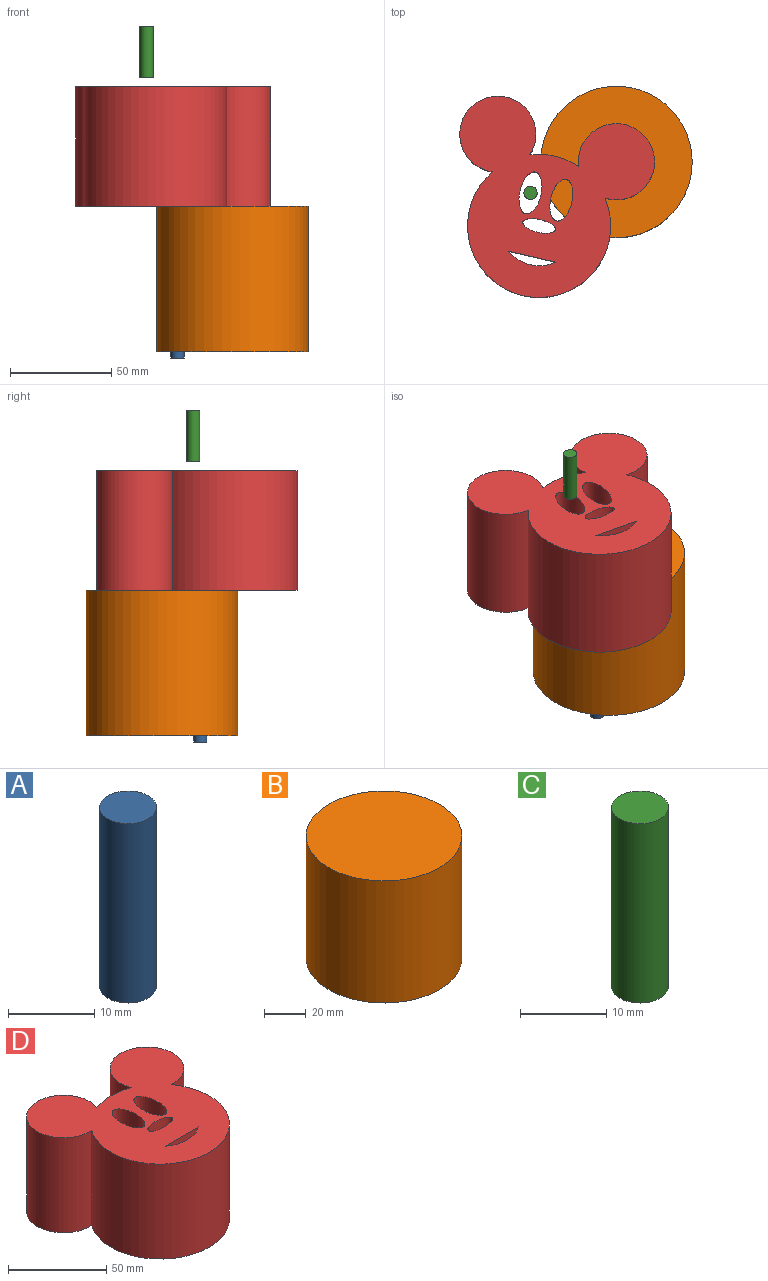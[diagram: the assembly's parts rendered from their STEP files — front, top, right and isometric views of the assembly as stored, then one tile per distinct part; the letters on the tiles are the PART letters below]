
ASSEMBLY  parts=4 mates=3
PART A: 3 faces, bbox 6.6x6.6x25.4 mm
  f0: cylinder r=3.29mm len=25.4mm, axis (0,0,-1), area 524.7mm2, adj f1,f2
  f1: plane 6.58x6.58mm, normal (0,0,1), area 34mm2, adj f0
  f2: plane 6.58x6.58mm, normal (0,0,-1), area 34mm2, adj f0
PART B: 3 faces, bbox 74.9x74.9x71.9 mm
  f0: cylinder r=37.46mm len=74.93mm, axis (0,0,-1), area 16913.7mm2, adj f1,f2
  f1: plane 74.93x74.93mm, normal (0,0,1), area 4409.5mm2, adj f0
  f2: plane 74.93x74.93mm, normal (0,0,-1), area 4409.5mm2, adj f0
PART C: 3 faces, bbox 6.6x6.6x25.4 mm
  f0: cylinder r=3.29mm len=25.4mm, axis (0,0,-1), area 524.7mm2, adj f1,f2
  f1: plane 6.58x6.58mm, normal (0,0,1), area 34mm2, adj f0
  f2: plane 6.58x6.58mm, normal (0,0,-1), area 34mm2, adj f0
PART D: 11 faces, bbox 97.9x93.8x59.3 mm
  f0: cylinder r=18.85mm len=59.28mm, axis (0,0,-1), area 5740.7mm2, adj f1,f8,f9,f10
  f1: cylinder r=35.41mm len=70.81mm, axis (0,0,-1), area 9228.2mm2, adj f0,f2,f9,f10
  f2: cylinder r=18.85mm len=59.28mm, axis (0,0,-1), area 5740.7mm2, adj f1,f8,f9,f10
  f3: cylinder r=19.69mm len=59.28mm, axis (0,0,-1), area 1532.4mm2, adj f7,f9,f10
  f4: extruded ~59.28x21.14mm, area 3040mm2, adj f9,f10
  f5: extruded ~59.28x21.14mm, area 3040mm2, adj f9,f10
  f6: extruded ~59.28x16.47mm, area 2240.3mm2, adj f9,f10
  f7: plane 59.28x24.03mm, normal (0,-1,0), area 1424.6mm2, adj f3,f9,f10
  f8: cylinder r=35.41mm len=59.28mm, axis (0,0,-1), area 1502.2mm2, adj f0,f2,f9,f10
  f9: plane 97.95x93.83mm, normal (0,0,1), area 5542.1mm2, adj f0,f1,f2,f3,f4,f5,f6,f7
  f10: plane 97.95x93.83mm, normal (0,0,-1), area 5542.1mm2, adj f0,f1,f2,f3,f4,f5,f6,f7
PLACE A rot(axis=(-0.11,-0.99,0),180deg) t=(-170.2,-168.49,45.69)mm
PLACE B rot(axis=(0,0,1),64.2deg) t=(-126.96,-0.54,23.41)mm fixed
PLACE C rot(axis=(-0.11,-0.99,0),180deg) t=(-170.11,-168.51,184.55)mm
PLACE D rot(axis=(-0.11,-0.99,0),180deg) t=(-171.21,-173.07,154.54)mm
MATE revolute D.f0 <-> B.f0  axis (0,0,-1) through (-132.93,-141.31,95.26)mm
MATE slider A.f0 <-> D.f10  axis (0,0,-1) through (-160.2,-160.28,20.29)mm
MATE slider C.f0 <-> D.f10  axis (0,0,-1) through (-175.48,-156.74,159.15)mm
